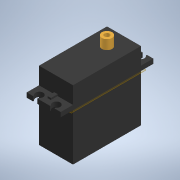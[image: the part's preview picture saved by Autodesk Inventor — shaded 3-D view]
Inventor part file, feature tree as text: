
AUTODESK INVENTOR PART (.ipt)
format: ipt  version: 2020 (Build 240168000, 168)  size: 204,288 bytes
history: native  units: in
note: dims shown in document units (in); Inventor stores cm internally (conversion verified against a paired STEP export)
features: extrude x6, sketch x6, projected_geometry x3, plane x1
ambient origin geometry x8: Origin, YZ Plane, XZ Plane, XY Plane, X Axis, Y Axis, Z Axis, Center Point
bodies: Solid1 (feature_tree)
feature tree (16):
  extrude  "Extrusion1"  Depth=1.5748in
  plane  "Work Plane1"
  extrude  "Extrusion2"  TaperAngle=0.0deg  [1 undecoded]
  extrude  "Extrusion3"  Depth=2.1457in
  extrude  "Extrusion4"  Depth=0.3937in
  extrude  "Extrusion5"  Depth=0.1063in TaperAngle=0.0deg
  extrude  "Extrusion6"  Depth=0.0787in
  sketch  "Sketch1"  dims[d0=0.7874in d1=1.5748in]
  sketch  "Sketch2"  dims[d2=1.0906in d3=0.0in d4=0.0in]
  projected_geometry  "Projected Loop1"
  sketch  "Sketch3"  dims[d5=0.5in d6=0.0in d7=2.1457in]
  projected_geometry  "Projected Loop2"
  sketch  "Sketch4"  dims[d8=0.3937in d9=1.9488in]
  sketch  "Sketch5"  dims[d10=0.1772in d11=0.1063in d12=0.0in]
  projected_geometry  "Projected Loop3"
  sketch  "Sketch6"  dims[d13=0.0984in d14=0.0787in d15=0.1575in d16=0.0394in d17=0.0in d18=0.2362in d19=1.1811in d20=0.2205in d21=0.0in d22=0.1181in d23=0.2205in d24=0.0in]
note: 1 required parameter value undecoded (feature->parameter linkage not recoverable at this tier; creation-order binding heuristic only, values carry confidence <= 0.55)
